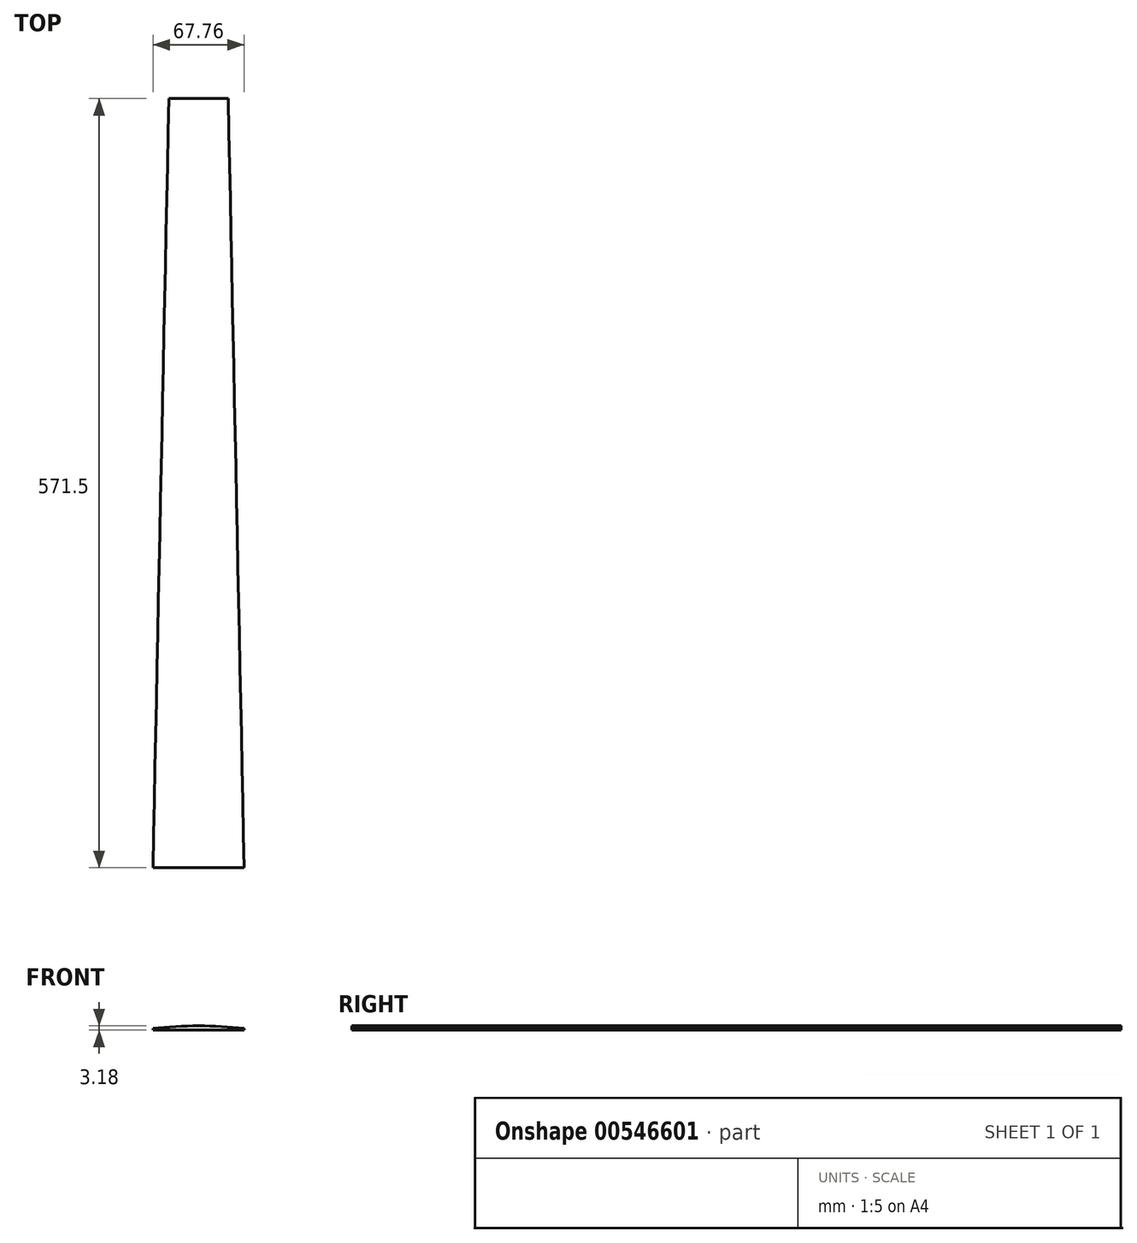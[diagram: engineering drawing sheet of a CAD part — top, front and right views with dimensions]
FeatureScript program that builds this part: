
annotation { "Feature Type Name" : "Feature", "Feature Type Description" : "" }
export const myFeature = defineFeature(function(context is Context, id is Id, definition is map)
    precondition{}
    {
        {
            var Q0;
            Q0=qCreatedBy(makeId("Top.planeOp"),FACE);
            var sketch = newSketch(context, id + "F0", { "sketchPlane" : qUnion([Q0])});
            skPoint(sketch, "E0.endSnap0", {"position": v(0, 0) * mm});
            skLineSegment(sketch, "E1", {"start": v(-22.07, 571.5) * mm, "end": v(22.07, 571.5) * mm});
            skLineSegment(sketch, "E2", {"start": v(22.07, 571.5) * mm, "end": v(33.88, 0) * mm});
            skLineSegment(sketch, "E3", {"start": v(33.88, 0) * mm, "end": v(-33.88, 0) * mm});
            skLineSegment(sketch, "E4", {"start": v(-33.88, 0) * mm, "end": v(-22.07, 571.5) * mm});
            skSolve(sketch);
        }
        {
            var Q0;
            Q0=qSketchRegion(id+"F0",true);
            extrude(context, id + "F1", {"entities" : qUnion([Q0]), "depth" : 3.17 * mm});
        }
        {
            var Q0;
            Q0=makeQuery(id+"F1.opExtrude","SWEPT_FACE",FACE,{"disambiguationData":[OSD([sQuery(id+"F0.wireOp",EDGE,"E3")])]});
            var sketch = newSketch(context, id + "F2", { "sketchPlane" : qUnion([Q0])});
            skArc(sketch, "E5", {"start": v(33.88, 1.29) * mm, "mid": v(0, 3.17) * mm, "end": v(-33.88, 1.29) * mm});
            skLineSegment(sketch, "E6", {"start": v(-33.88, 1.29) * mm, "end": v(-33.88, 3.18) * mm});
            skLineSegment(sketch, "E7", {"start": v(-33.88, 3.18) * mm, "end": v(33.88, 3.18) * mm});
            skLineSegment(sketch, "E8", {"start": v(33.88, 3.18) * mm, "end": v(33.88, 1.29) * mm});
            skSolve(sketch);
        }
        {
            var Q0;
            Q0=qSketchRegion(id+"F2",true);
            extrude(context, id + "F3", {"entities" : qUnion([Q0]), "operationType" : NewBodyOperationType.REMOVE, "endBound" : BoundingType.THROUGH_ALL, "oppositeDirection" : true, "depth" : 25.4 * mm});
        }
    });
